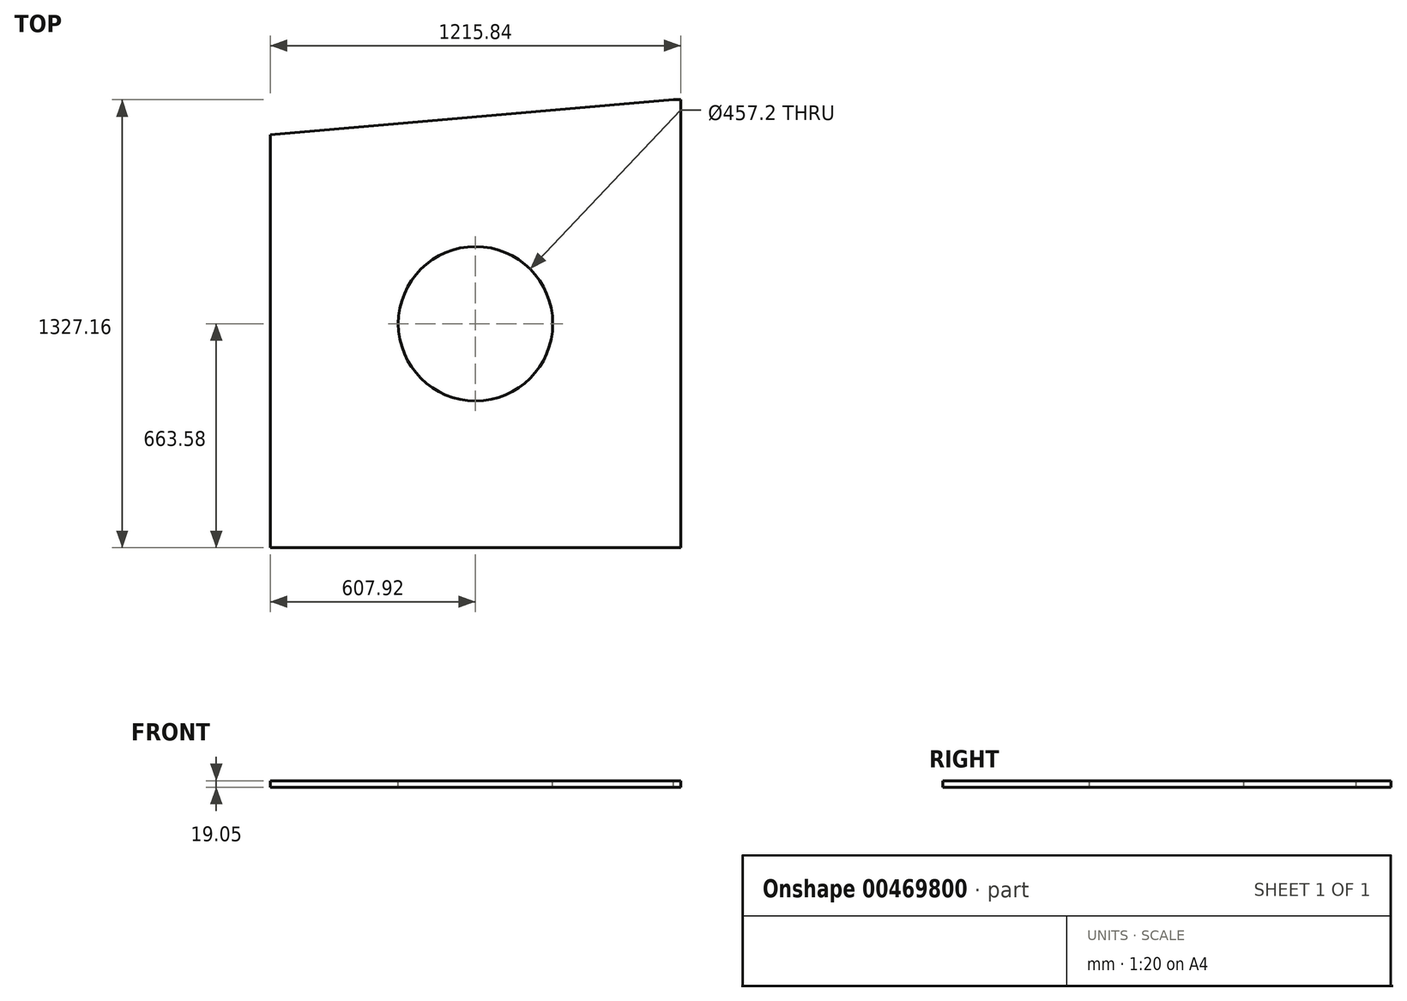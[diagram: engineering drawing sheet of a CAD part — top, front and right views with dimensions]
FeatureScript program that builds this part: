
annotation { "Feature Type Name" : "Feature", "Feature Type Description" : "" }
export const myFeature = defineFeature(function(context is Context, id is Id, definition is map)
    precondition{}
    {
        {
            var Q0;
            Q0=qCreatedBy(makeId("Top.planeOp"),FACE);
            var sketch = newSketch(context, id + "F0", { "sketchPlane" : qUnion([Q0])});
            skLineSegment(sketch, "E0.bottom", {"start": v(-607.92, -663.58) * mm, "end": v(607.92, -663.58) * mm});
            skLineSegment(sketch, "E0.top", {"start": v(-607.92, 663.58) * mm, "end": v(607.92, 663.58) * mm});
            skLineSegment(sketch, "E0.left", {"start": v(-607.92, -663.58) * mm, "end": v(-607.92, 663.58) * mm});
            skLineSegment(sketch, "E0.right", {"start": v(607.92, -663.58) * mm, "end": v(607.92, 663.58) * mm});
            skPoint(sketch, "E0.middle", {"position": v(0, 0) * mm});
            skSolve(sketch);
        }
        {
            var Q0;
            Q0=qSketchRegion(id+"F0",true);
            extrude(context, id + "F1", {"entities" : qUnion([Q0]), "depth" : 19.05 * mm});
        }
        {
            var Q0;
            Q0=makeQuery(id+"F1.opExtrude","SWEPT_EDGE",EDGE,{"disambiguationData":[OSD([sQuery(id+"F0.wireOp",EDGE,"E0.top"),sQuery(id+"F0.wireOp",EDGE,"E0.left")])]});
            chamfer(context, id + "F2", {"entities" : qUnion([Q0]), "chamferType" : ChamferType.OFFSET_ANGLE, "width" : 1193.52 * mm, "oppositeDirection" : true, "angle" : 5 * degree, "tangentPropagation" : true});
        }
        {
            var Q0;
            Q0=makeQuery(id+"F1.opExtrude","CAP_FACE",FACE,{"disambiguationData":[OSD([sQuery(id+"F0.wireOp",EDGE,"E0.bottom"),sQuery(id+"F0.wireOp",EDGE,"E0.top"),sQuery(id+"F0.wireOp",EDGE,"E0.left"),sQuery(id+"F0.wireOp",EDGE,"E0.right")])],"isStart":false});
            var sketch = newSketch(context, id + "F3", { "sketchPlane" : qUnion([Q0])});
            skCircle(sketch, "E1", {"center": v(0, 0) * mm, "radius": 228.6 * mm});
            skSolve(sketch);
        }
        {
            var Q0;
            Q0=qSketchRegion(id+"F3",true);
            extrude(context, id + "F4", {"entities" : qUnion([Q0]), "operationType" : NewBodyOperationType.REMOVE, "endBound" : BoundingType.THROUGH_ALL, "oppositeDirection" : true, "depth" : 25.4 * mm});
        }
    });
